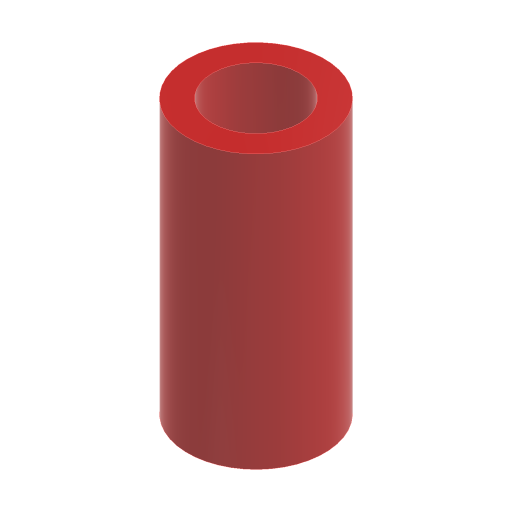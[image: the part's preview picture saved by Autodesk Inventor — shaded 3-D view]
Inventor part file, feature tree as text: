
AUTODESK INVENTOR PART (.ipt)
format: ipt  version: 2024.3 (Build 283343000, 343)  size: 246,272 bytes
history: native  units: mm
features: extrude x1, sketch x1
ambient origin geometry x8: Origin, YZ Plane, XZ Plane, XY Plane, X Axis, Y Axis, Z Axis, Center Point
bodies: Solid1 (feature_tree)
feature tree (2):
  extrude  "Extrusion1"  Depth=11.0mm
  sketch  "Sketch1"  dims[d0=3.5mm d1=1.0mm d2=11.0mm d3=0.0mm]
